# Revit family: LF6SQ
name_source: partatom
category: Lighting Fixtures
revit_build: Autodesk Revit 2014 (Build: 20130308_1515(x64)
units: mm (PartAtom-declared; Revit-internal decimal feet)

## types (1)
- LF6SQ
    Apparent Load = 33 VA
    Assembly Code = D5020200
    Color Filter = 16777215
    Connector Description = Lighting
    Default Elevation = 48"
    Description = LF6SQ is a 6inch architectural LED square downlight designed with a 6 degree rotation adjustment to ensure perfect alignment after installation.
    Dimming Lamp Color Temperature Shift = <None>
    Emit Shape Visible in Rendering = No
    Emit from Rectangle Length = 6"
    Emit from Rectangle Width = 6"
    Glass = Glass - Hubbell - White Glass
    Height = 5 1/2"
    Housing Options = Emergency Battery Pack with remote test switch and indicator light
    Housing options = Emergency Battery Pack
with remote test switch
and indicator light
    Lamp = 1
    Length = 14"
    Load Classification = Lighting
    Manufacturer = Prescolite
    Model = LF6SQLED
    Mounting = Recessed
    Number of Poles = 1
    Photometric Link = https://www.hubbell.com
    Photometric Notes = More IES files download on Photometric Link
    Photometric Web File = LF6SQML-6SQML30L30K8.IES
    Power Factor = 0.9
    Product Documentation Link = https://hubbellcdn.com
    Product Material = Metal - Hubbell - Steel
    Product Page URL = https://www.hubbell.com
    Tilt Angle = -90.00°
    Type Comments = Light Fixture
    URL = https://www.hubbell.com
    Voltage = 120 V
    Warranty = 5-Years Warranty
    Wattage Comments = 33
    Width = 12 5/8"

## geometry (parser evidence)
native form markers: Blend x4, Sweep x3
no freeform markers — native parametric forms only
